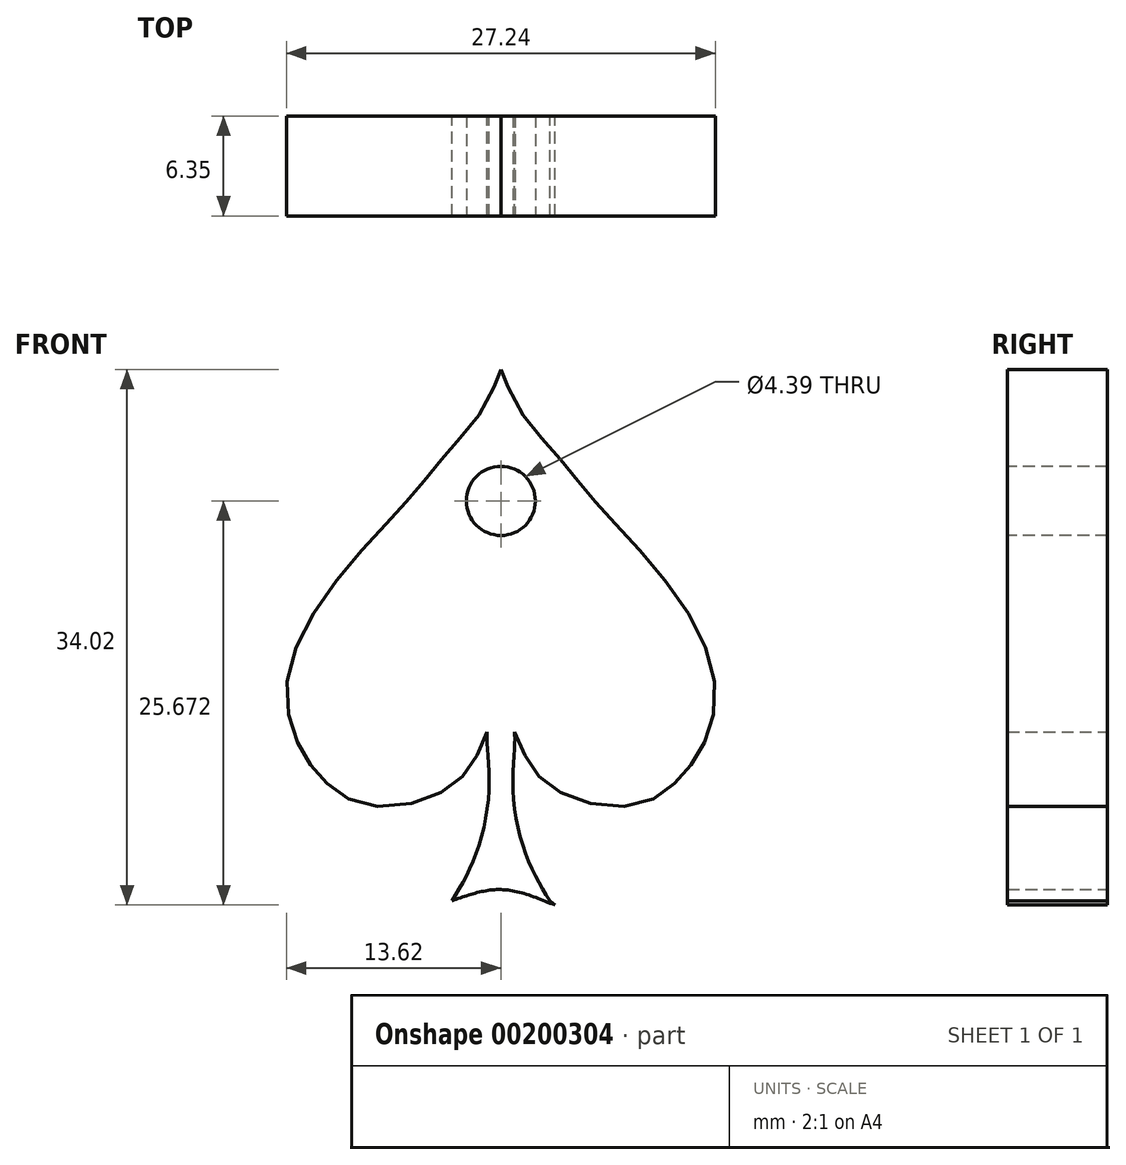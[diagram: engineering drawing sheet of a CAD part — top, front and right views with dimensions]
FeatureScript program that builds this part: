
annotation { "Feature Type Name" : "Feature", "Feature Type Description" : "" }
export const myFeature = defineFeature(function(context is Context, id is Id, definition is map)
    precondition{}
    {
        {
            var Q0;
            Q0=qCreatedBy(makeId("Front.planeOp"),FACE);
            var sketch = newSketch(context, id + "F0", { "sketchPlane" : qUnion([Q0])});
            skFitSpline(sketch, "E0", {"points": [v(-3.11, -14.78) * mm, v(0, -14.07) * mm, v(3.42, -15.05) * mm], "startDerivative": vector(6.33, 2.3) * mm, "endDerivative": vector(6.73, -2.79) * mm});
            skFitSpline(sketch, "E1", {"points": [v(-0.87, -4.04) * mm, v(-0.87, -4.84) * mm, v(-0.78, -8.16) * mm, v(-1.77, -12.28) * mm, v(-3.11, -14.78) * mm], "startDerivative": vector(-0.19, -4.82) * mm, "endDerivative": vector(-5.4, -8.85) * mm});
            skFitSpline(sketch, "E2", {"points": [v(-0.87, -4.04) * mm, v(-2.09, -6.46) * mm, v(-4.54, -8.25) * mm, v(-8.93, -8.6) * mm, v(-11.35, -7) * mm, v(-12.87, -4.84) * mm, v(-13.59, -1) * mm, v(-11.44, 4.2) * mm, v(-7.5, 8.94) * mm, v(-5.17, 11.54) * mm, v(-3.11, 14.05) * mm, v(-0.87, 16.91) * mm, v(0, 18.97) * mm, v(0, 18.88) * mm], "startDerivative": vector(-14.19, -35.68) * mm, "endDerivative": vector(-0.94, -10.38) * mm});
            skFitSpline(sketch, "E3.MirrorCS", {"points": [v(0.87, -4.04) * mm, v(0.87, -4.84) * mm, v(0.78, -8.16) * mm, v(1.77, -12.28) * mm, v(3.11, -14.78) * mm], "startDerivative": vector(0.19, -4.82) * mm, "endDerivative": vector(5.4, -8.85) * mm});
            skFitSpline(sketch, "E4.MirrorCS", {"points": [v(0.87, -4.04) * mm, v(2.09, -6.46) * mm, v(4.54, -8.25) * mm, v(8.93, -8.6) * mm, v(11.35, -7) * mm, v(12.87, -4.84) * mm, v(13.59, -1) * mm, v(11.44, 4.2) * mm, v(7.5, 8.94) * mm, v(5.17, 11.54) * mm, v(3.11, 14.05) * mm, v(0.87, 16.91) * mm, v(0, 18.97) * mm, v(0, 18.88) * mm], "startDerivative": vector(14.19, -35.68) * mm, "endDerivative": vector(0.94, -10.38) * mm});
            skLineSegment(sketch, "E5", {"start": v(3.11, -14.78) * mm, "end": v(3.42, -15.05) * mm});
            skLineSegment(sketch, "E6", {"start": v(24.1, 18.93) * mm, "end": v(24.1, -15.05) * mm});
            skLineSegment(sketch, "E7", {"start": v(0, 18.93) * mm, "end": v(0, -14.07) * mm});
            skSolve(sketch);
        }
        {
            var Q0;
            Q0 = qSketchRegion(id + "F0", true);
            extrude(context, id + "F1", {"entities" : qUnion([Q0]), "depth" : 6.35 * mm});
        }
        {
            var Q0;
            Q0=makeQuery(id+"F1.opExtrude","CAP_FACE",FACE,{"disambiguationData":[OSD([sQuery(id+"F0.wireOp",EDGE,"E0"),sQuery(id+"F0.wireOp",EDGE,"E1"),sQuery(id+"F0.wireOp",EDGE,"E2"),sQuery(id+"F0.wireOp",EDGE,"E3.MirrorCS"),sQuery(id+"F0.wireOp",EDGE,"E4.MirrorCS"),sQuery(id+"F0.wireOp",EDGE,"E5")])],"isStart":false});
            var sketch = newSketch(context, id + "F2", { "sketchPlane" : qUnion([Q0])});
            skCircle(sketch, "E8", {"center": v(0, 10.62) * mm, "radius": 2.2 * mm});
            skSolve(sketch);
        }
        {
            var Q0;
            Q0=makeQuery(id+"F2.imprint","IMPRINT",FACE,{"disambiguationData":[TD([[makeQuery(id+"F2.imprint","IMPRINT",EDGE,{"derivedFrom":sQuery(id+"F2.wireOp",EDGE,"E8")}),1.0]])]});
            extrude(context, id + "F3", {"entities" : qUnion([Q0]), "operationType" : NewBodyOperationType.REMOVE, "oppositeDirection" : true, "depth" : 25.4 * mm});
        }
    });
